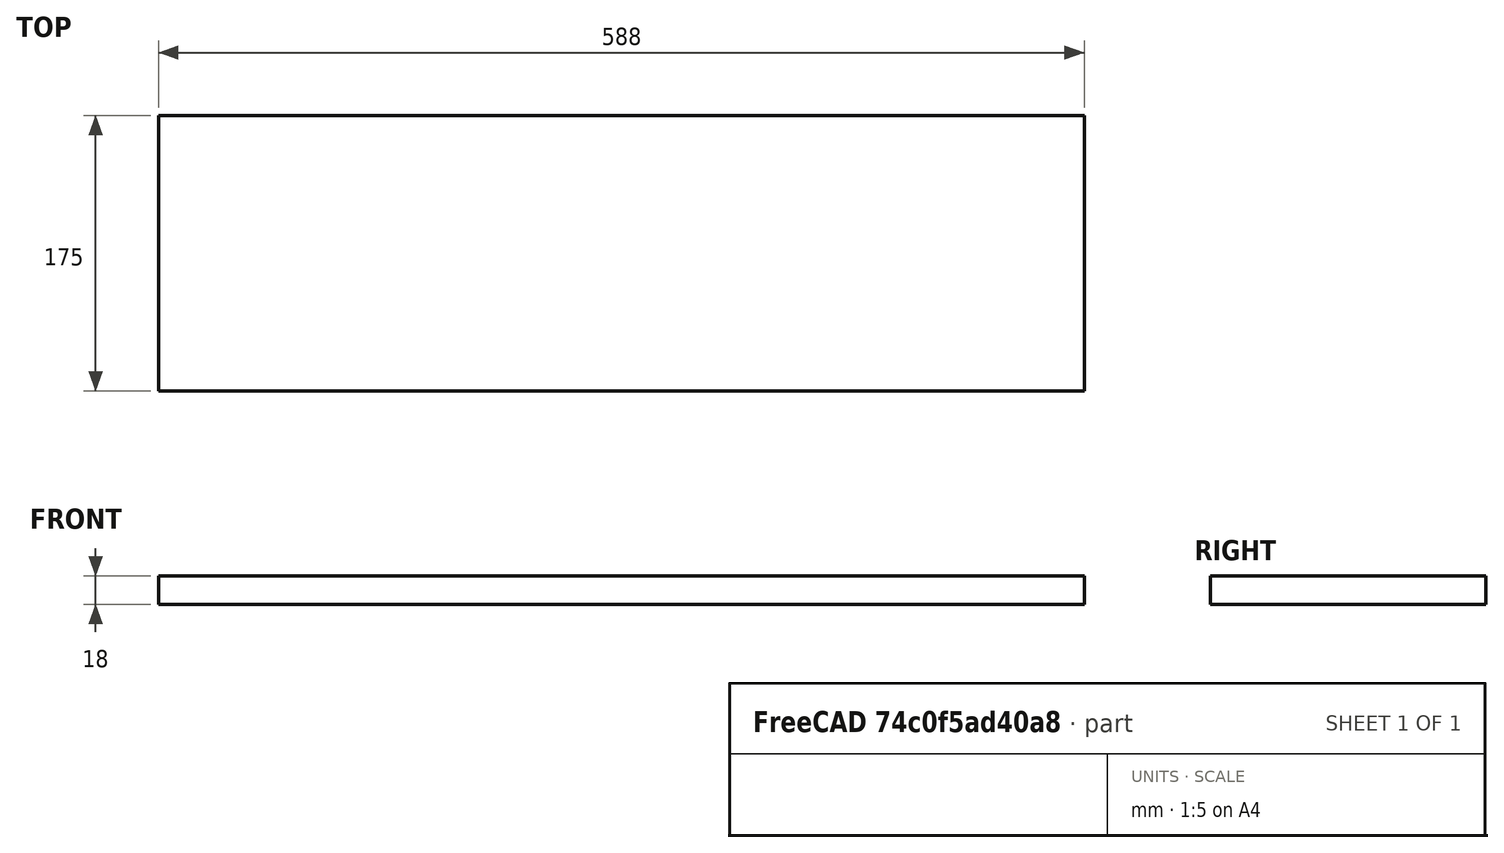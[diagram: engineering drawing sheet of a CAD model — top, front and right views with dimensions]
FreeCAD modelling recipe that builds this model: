
FCSTD DOCUMENT  (FreeCAD 1.0R39109 (Git))
Label: 14_shelf_trays
License: All rights reserved
LicenseURL: http://en.wikipedia.org/wiki/All_rights_reserved
objects: Spreadsheet::Sheet×1, Sketcher::SketchObject×1, PartDesign::Pad×1, PartDesign::Body×1
note: 6 computed .brp shape members not serialized (recipe doc carries the construction recipe); baked Part::Feature solids carry a one-line shape summary decoded from their .brp

FEATURE [Spreadsheet::Sheet] Spreadsheet
  cells = A2='length; B2(length)=588; A3='width; B3(width)=175; A4='height; B4(height)=18
FEATURE [Sketcher::SketchObject] Sketch
  ArcFitTolerance = 0
  AttachmentSupport = -> [XY_Plane]
  FullyConstrained = true
  MakeInternals = false
  MapMode = 5
  expr: Constraints[11] = Spreadsheet.length
  expr: Constraints[12] = Spreadsheet.width
  sketch-geometry (5):
    g0: LineSegment StartX=-294 StartY=87.5 StartZ=0 EndX=294 EndY=87.5 EndZ=0
    g1: LineSegment StartX=294 StartY=87.5 StartZ=0 EndX=294 EndY=-87.5 EndZ=0
    g2: LineSegment StartX=294 StartY=-87.5 StartZ=0 EndX=-294 EndY=-87.5 EndZ=0
    g3: LineSegment StartX=-294 StartY=-87.5 StartZ=0 EndX=-294 EndY=87.5 EndZ=0
    g4: LineSegment [constr] StartX=-294 StartY=87.5 StartZ=0 EndX=294 EndY=-87.5 EndZ=0
  constraints (13):
    c: Coincident(g0,g1)
    c: Coincident(g1,g2)
    c: Coincident(g2,g3)
    c: Coincident(g3,g0)
    c: Horizontal(g0)
    c: Horizontal(g2)
    c: Vertical(g1)
    c: Vertical(g3)
    c: Coincident(g4,g1)
    c: Coincident(g0,g4)
    c: Symmetric(g0,g1,g-1)
    c: Distance(g0,g0) = 588
    c: Distance(g0,g2) = 175
FEATURE [PartDesign::Pad] Pad
  Direction = (0,0,1)
  Length = 18
  Length2 = 10
  Profile = -> Sketch
  ReferenceAxis = -> Sketch [N_Axis]
  Suppressed = false
  Type = 0
  expr: Length = Spreadsheet.height
FEATURE [PartDesign::Body] Body
  AllowCompound = false
  Group = -> [Sketch,Pad]
  Origin = -> Origin
  Tip = -> Pad
